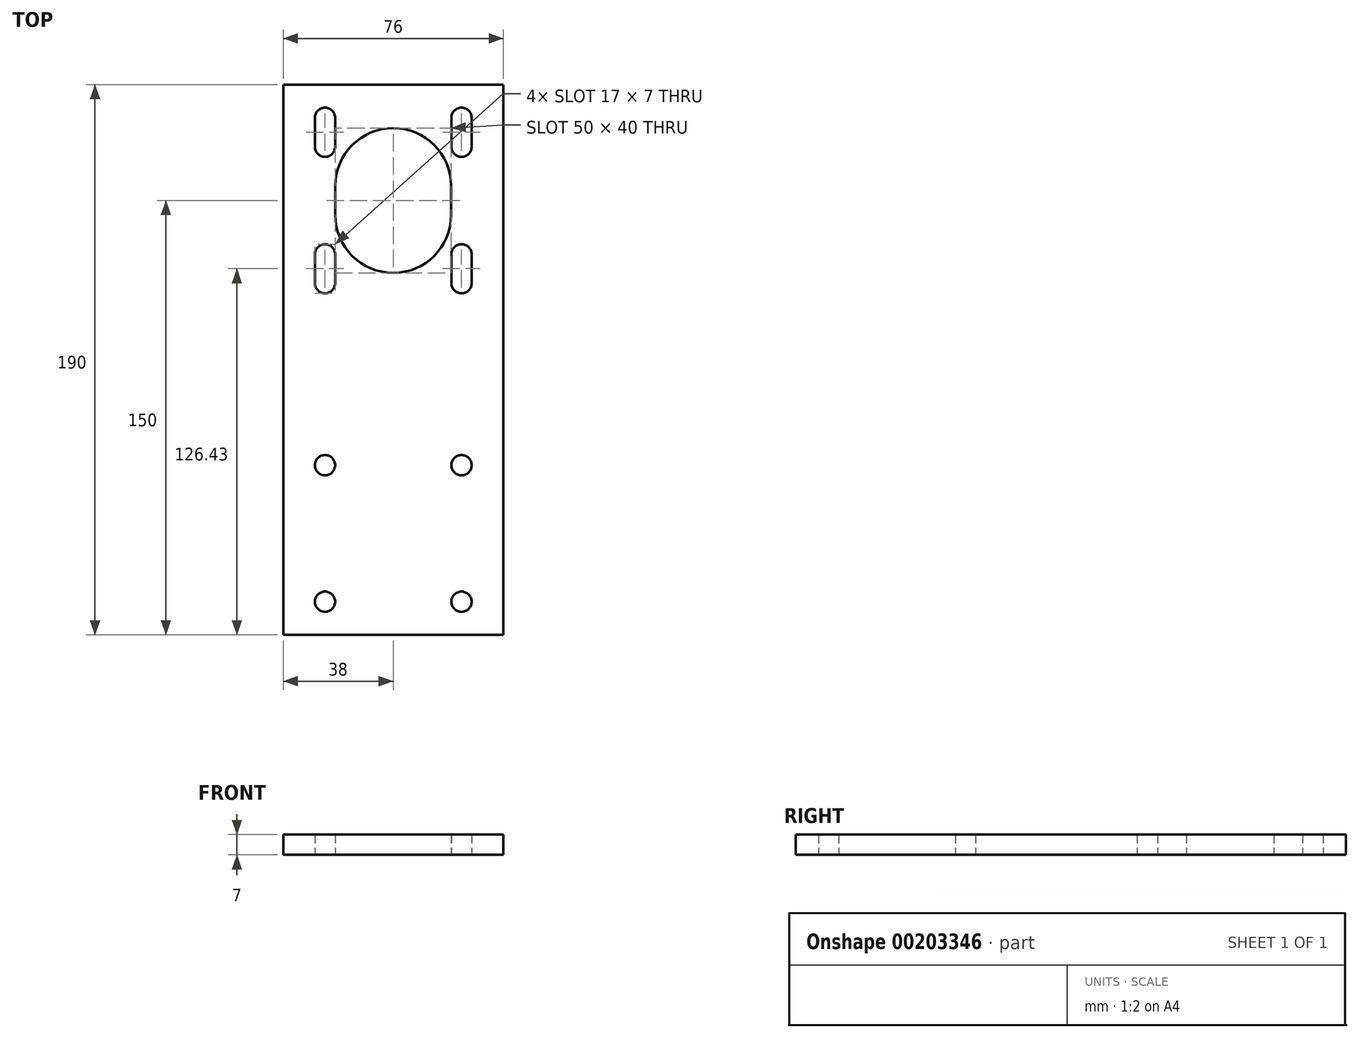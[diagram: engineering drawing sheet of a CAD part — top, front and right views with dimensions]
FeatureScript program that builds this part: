
annotation { "Feature Type Name" : "Feature", "Feature Type Description" : "" }
export const myFeature = defineFeature(function(context is Context, id is Id, definition is map)
    precondition{}
    {
        {
            var Q0;
            Q0=qCreatedBy(makeId("Top.planeOp"),FACE);
            var sketch = newSketch(context, id + "F0", { "sketchPlane" : qUnion([Q0])});
            skCircle(sketch, "E0", {"center": v(0, 0) * mm, "radius": 20 * mm});
            skLineSegment(sketch, "E1", {"start": v(-20, 120) * mm, "end": v(-20, 110) * mm});
            skLineSegment(sketch, "E2", {"start": v(20, 120) * mm, "end": v(20, 110) * mm});
            skArc(sketch, "E3", {"start": v(-20, 120) * mm, "mid": v(0, 140) * mm, "end": v(20, 120) * mm});
            skArc(sketch, "E4", {"start": v(-20, 110) * mm, "mid": v(0, 90) * mm, "end": v(20, 110) * mm});
            skLineSegment(sketch, "E5.bottom", {"start": v(38, -35) * mm, "end": v(-38, -35) * mm});
            skLineSegment(sketch, "E5.top", {"start": v(38, 155) * mm, "end": v(-38, 155) * mm});
            skLineSegment(sketch, "E5.left", {"start": v(38, -35) * mm, "end": v(38, 155) * mm});
            skLineSegment(sketch, "E5.right", {"start": v(-38, -35) * mm, "end": v(-38, 155) * mm});
            skPoint(sketch, "E5.middle", {"position": v(0, 60) * mm});
            skCircle(sketch, "E6", {"center": v(-23.57, -23.57) * mm, "radius": 3.5 * mm});
            skCircle(sketch, "E7.0.1.0", {"center": v(-23.57, 23.57) * mm, "radius": 3.5 * mm});
            skCircle(sketch, "E7.1.0.0", {"center": v(23.57, -23.57) * mm, "radius": 3.5 * mm});
            skCircle(sketch, "E7.1.1.0", {"center": v(23.57, 23.57) * mm, "radius": 3.5 * mm});
            skLineSegment(sketch, "E7.direction1", {"start": v(-23.57, -23.57) * mm, "end": v(23.57, -23.57) * mm, "construction": true});
            skLineSegment(sketch, "E7.direction2", {"start": v(-23.57, -23.57) * mm, "end": v(-23.57, 23.57) * mm, "construction": true});
            skLineSegment(sketch, "E8", {"start": v(-27.07, 96.43) * mm, "end": v(-27.07, 86.43) * mm});
            skLineSegment(sketch, "E9", {"start": v(-20.07, 96.43) * mm, "end": v(-20.07, 86.43) * mm});
            skArc(sketch, "E10", {"start": v(-27.07, 86.43) * mm, "mid": v(-23.57, 82.93) * mm, "end": v(-20.07, 86.43) * mm});
            skArc(sketch, "E11", {"start": v(-27.07, 96.43) * mm, "mid": v(-23.57, 99.93) * mm, "end": v(-20.07, 96.43) * mm});
            skLineSegment(sketch, "E12.0.1.0", {"start": v(-27.07, 143.57) * mm, "end": v(-27.07, 133.57) * mm});
            skArc(sketch, "E12.0.1.1", {"start": v(-27.07, 143.57) * mm, "mid": v(-23.57, 147.07) * mm, "end": v(-20.07, 143.57) * mm});
            skLineSegment(sketch, "E12.0.1.2", {"start": v(-20.07, 143.57) * mm, "end": v(-20.07, 133.57) * mm});
            skArc(sketch, "E12.0.1.3", {"start": v(-27.07, 133.57) * mm, "mid": v(-23.57, 130.07) * mm, "end": v(-20.07, 133.57) * mm});
            skLineSegment(sketch, "E12.1.0.0", {"start": v(20.07, 96.43) * mm, "end": v(20.07, 86.43) * mm});
            skArc(sketch, "E12.1.0.1", {"start": v(20.07, 96.43) * mm, "mid": v(23.57, 99.93) * mm, "end": v(27.07, 96.43) * mm});
            skLineSegment(sketch, "E12.1.0.2", {"start": v(27.07, 96.43) * mm, "end": v(27.07, 86.43) * mm});
            skArc(sketch, "E12.1.0.3", {"start": v(20.07, 86.43) * mm, "mid": v(23.57, 82.93) * mm, "end": v(27.07, 86.43) * mm});
            skLineSegment(sketch, "E12.1.1.0", {"start": v(20.07, 143.57) * mm, "end": v(20.07, 133.57) * mm});
            skArc(sketch, "E12.1.1.1", {"start": v(20.07, 143.57) * mm, "mid": v(23.57, 147.07) * mm, "end": v(27.07, 143.57) * mm});
            skLineSegment(sketch, "E12.1.1.2", {"start": v(27.07, 143.57) * mm, "end": v(27.07, 133.57) * mm});
            skArc(sketch, "E12.1.1.3", {"start": v(20.07, 133.57) * mm, "mid": v(23.57, 130.07) * mm, "end": v(27.07, 133.57) * mm});
            skLineSegment(sketch, "E12.direction1", {"start": v(-27.07, 86.43) * mm, "end": v(20.07, 86.43) * mm, "construction": true});
            skLineSegment(sketch, "E12.direction2", {"start": v(-27.07, 86.43) * mm, "end": v(-27.07, 133.57) * mm, "construction": true});
            skSolve(sketch);
        }
        {
            var Q0;
            Q0=makeQuery(id+"F0.imprint","IMPRINT",FACE,{"disambiguationData":[TD([[makeQuery(id+"F0.imprint","IMPRINT",EDGE,{"derivedFrom":sQuery(id+"F0.wireOp",EDGE,"E0")}),-1.0]])]});
            var Q1;
            Q1=makeQuery(id+"F0.imprint","IMPRINT",FACE,{"disambiguationData":[TD([[makeQuery(id+"F0.imprint","IMPRINT",EDGE,{"derivedFrom":sQuery(id+"F0.wireOp",EDGE,"b26efcef-8d49-46b2-9c06-3a571744681e.0")}),1.0]])]});
            var Q2;
            Q2=makeQuery(id+"F0.imprint","IMPRINT",FACE,{"disambiguationData":[TD([[makeQuery(id+"F0.imprint","IMPRINT",EDGE,{"derivedFrom":sQuery(id+"F0.wireOp",EDGE,"4311d710-d6d6-46f8-bc42-06a2a10d98ef.0")}),-1.0]])]});
            var Q3;
            {var subQ0=sQuery(id+"F0.wireOp",EDGE,"MgP6AME8-mGq3-Rid9-JIhx-g5hkLvP5y9p3.bottom");var subQ1=sQuery(id+"F0.wireOp",EDGE,"E0");var subQ2=makeQuery(id+"F0.imprint","INTERSECT",VERTEX,{"derivedFrom":[subQ1,subQ0]});Q3=makeQuery(id+"F0.imprint","IMPRINT",FACE,{"disambiguationData":[TD([[makeQuery(id+"F0.imprint","IMPRINT",EDGE,{"disambiguationData":[TD([[subQ2,-1.0]])],"derivedFrom":subQ1}),1.0]])]});}
            var Q4;
            {var subQ5=sQuery(id+"F0.wireOp",EDGE,"p5bBgsXZ-vagG-Ory5-czZu-PTXsH0Fwks5G.left");Q4=makeQuery(id+"F0.imprint","IMPRINT",FACE,{"disambiguationData":[TD([[makeQuery(id+"F0.imprint","IMPRINT",EDGE,{"derivedFrom":subQ5}),1.0]])]});}
            var Q5;
            {var subQ5=sQuery(id+"F0.wireOp",EDGE,"p5bBgsXZ-vagG-Ory5-czZu-PTXsH0Fwks5G.right");Q5=makeQuery(id+"F0.imprint","IMPRINT",FACE,{"disambiguationData":[TD([[makeQuery(id+"F0.imprint","IMPRINT",EDGE,{"derivedFrom":subQ5}),-1.0]])]});}
            extrude(context, id + "F1", {"entities" : qUnion([Q0, Q1, Q2, Q3, Q4, Q5]), "depth" : 7 * mm});
        }
    });
